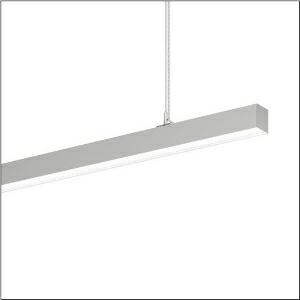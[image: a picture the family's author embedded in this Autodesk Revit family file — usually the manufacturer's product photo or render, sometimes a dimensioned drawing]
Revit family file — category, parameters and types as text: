
# Revit family: silica_r__21_51mx30tat4s_875d
name_source: partatom
category: Lighting Fixtures
units: mm (PartAtom-declared; Revit-internal decimal feet)

## family parameters
Cut with Voids When Loaded = No
Host = Face
Light Source = No
Part Type = Normal
Room Calculation Point = No
Round Connector Dimension = Use Diameter
Shared = No

## types (1)
- --- (1 x LED, 4120 lm, 33.8 W, 6500K)
    Apparent Load = 34 VA
    CIE Flux Codes = 47 79 96 58 100
    Color Rendering = 80
    Color Temperature = 6500K
    Default Elevation = 1800 mm
    Description = Silica® 21, office luminaire, primary optical cover: cover, of PMMA, opal, light emission: direct/indirect distribution, primary light characteristic: symmetric, installation type: suspended mounting, LED, rated luminous flux: 4.120lm, luminous efficacy: 116lm/W, light colour: 8tw, colour temperature: 2700..6500K, control gear: ECG DALI, with terminal, 3+2-pole, max. 2.5mm², mains connection: 220..240V, AC, 50/60Hz, rated input power: 35.5W, luminaire housing, of aluminium, metallic grey (RAL 9006), length: 1.204mm, width: 53mm, height: 53mm, protection rating (complete): IP20, insulation class (complete): insulation class I (protective earthing), certification: CE, permissible operating ambient temperature: 0..+35°C, standard: EN 50419, packaging unit: 1 piece
    Height = 53 mm
    Lamp = 1 x LED
    Lamp Light Flux = 4120 lm
    Lamp Power = 33.8 W
    Lamp count = 1
    Length = 1204 mm
    Luminous efficacy = 122 lm/W
    Manufacturer = Siteco
    ModVariant = No
    Model = 51MX30TAT4S
    Mounting Place = Ceiling
    Mounting Type = Pendant
    Number of Poles = 1
    OnlyDefault = Yes
    Power Factor = 1
    Product Name = Silica® 21
    Product group = office luminaire | ceiling pendant
    ProductGroupID = 905
    Protection Class = Protection class I
    Protection Degree = IP 20
    RLX_Detail_Level = 1
    RlxData = <blob elided: 20133 chars, md5=4631dfa7>
    Socket = socket
    Standby Power = 0 W
    System Light Flux = 4120 lm
    System Power = 34 W
    Type Comments = individual setting
    Type Image = l_1251727.jpg
    URL = http://relux.com
    VarID = @adj_045711
    Voltage = 0 V
    Weight = 0.00 kg
    Width = 53 mm

## geometry (parser evidence)
native form markers: Blend x4, Sweep x14
no freeform markers — native parametric forms only
